# Revit family: CRS-3555
name_source: partatom
category: Lighting Fixtures
units: mm (PartAtom-declared; Revit-internal decimal feet)

## family parameters
Always vertical = Yes
Cut with Voids When Loaded = No
Host = Ceiling
Light Source = Yes
OmniClass Number = 23.80.70.11.14.17
OmniClass Title = Direct/Indirect
Part Type = Normal
Room Calculation Point = No
Round Connector Dimension = Use Diameter
Shared = No

## types (7) — shared parameters
Assembly Code = D5020200
Color Filter = 16777215
Description = LED Cleanroom Surface Mount Inset Door
Dimming Lamp Color Temperature Shift = <None>
Emit Shape Visible in Rendering = No
Height = 0' - 4 1/16"
Housing Finish = Metal - Viscor - White
Lamp = LED
Lens Finish = Acrylic - Viscor - Frosted Prismatic P12
Manufacturer = CERTOLUX by VISCOR
Model = CRIS-3525
Tilt Angle = 90.00°
URL = https://www.viscor.com
Voltage = 120 V

## per-type parameters (varying)
| type | Apparent Load | Emit from Rectangle Length | Emit from Rectangle Width | Lamp Wattage | Length | Photometric Web File | Width |
| CRS-3555-2X2-LED840K035LUNV-P13 | 33 VA | 2' - 0" | 2' - 0" | 33 VA | 2' - 0" | CRS-3555-2X2-LED840K035LUNV-P13.ies | 2' - 0" |
| CRS-3555-2X4-LED840K104LUNV-P13 | 98 VA | 4' - 0" | 2' - 0" | 98 VA | 4' - 0" | CRS-3555-2X4-LED840K104LUNV-P13.ies | 2' - 0" |
| CRS-3555-1X4-LED840K104LUNV-P13 | 98 VA | 4' - 0" | 1' - 0" | 98 VA | 4' - 0" | CRS-3555-1X4-LED840K0104LUNV-P13.ies | 1' - 0" |
| CRS-3555-1X4-LED840K078LUNV-P13 | 75 VA | 4' - 0" | 1' - 0" | 75 VA | 4' - 0" | CRS-3555-1X4-LED840K078LUNV-P13.ies | 1' - 0" |
| CRS-3555-2X2-LED840K052LUNV-P13 | 47 VA | 2' - 0" | 2' - 0" | 47 VA | 2' - 0" | CRS-3555-2X2-LED840K052LUNV-P13.ies | 2' - 0" |
| CRS-3555-2X4-LED840K150LUNV-P13 | 147 VA | 4' - 0" | 2' - 0" | 147 VA | 4' - 0" | CRS-3555-2X4-LED840K150LUNV-P13.ies | 2' - 0" |
| CRS-3555-2X2-LED840K052LUNV-DSA | 47 VA | 2' - 0" | 2' - 0" | 47 VA | 2' - 0" | CRS-3555-2X2-LED840K052Lxxx-DSA.ies | 2' - 0" |

## geometry (parser evidence)
native form markers: Sweep x2
no freeform markers — native parametric forms only
